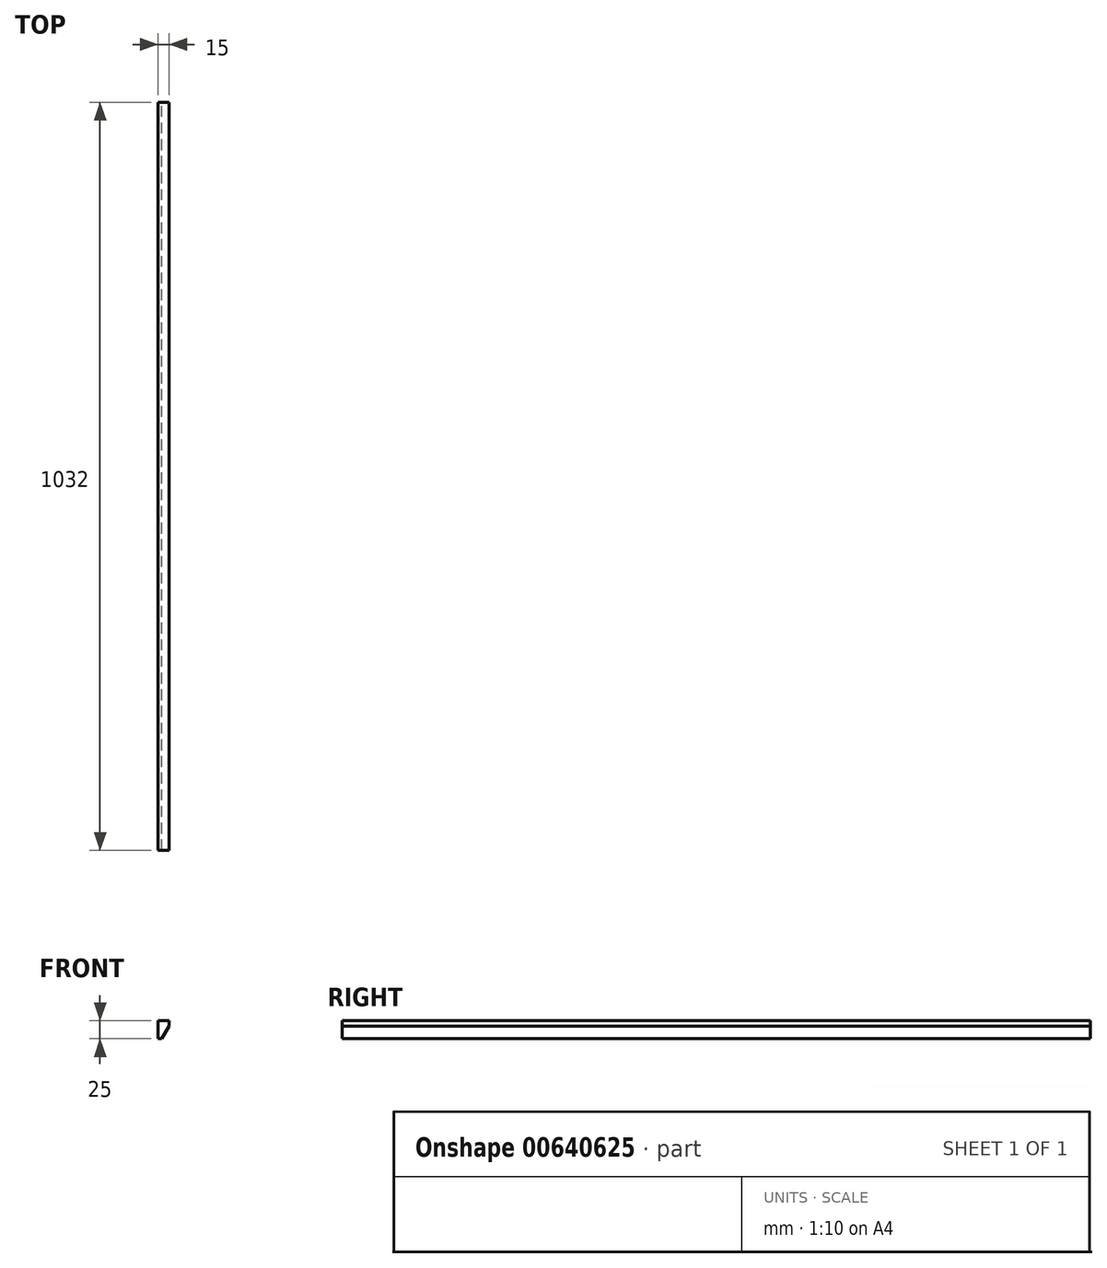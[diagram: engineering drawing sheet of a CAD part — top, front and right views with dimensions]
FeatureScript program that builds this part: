
annotation { "Feature Type Name" : "Feature", "Feature Type Description" : "" }
export const myFeature = defineFeature(function(context is Context, id is Id, definition is map)
    precondition{}
    {
        {
            var Q0;
            Q0=qCreatedBy(makeId("Front.planeOp"),FACE);
            var sketch = newSketch(context, id + "F0", { "sketchPlane" : qUnion([Q0])});
            skLineSegment(sketch, "E0.bottom", {"start": v(0, 0) * mm, "end": v(5, 0) * mm});
            skLineSegment(sketch, "E0.top", {"start": v(0, 25) * mm, "end": v(15, 25) * mm});
            skLineSegment(sketch, "E0.left", {"start": v(0, 0) * mm, "end": v(0, 25) * mm});
            skLineSegment(sketch, "E0.right", {"start": v(15, 17.32) * mm, "end": v(15, 25) * mm});
            skLineSegment(sketch, "E1", {"start": v(5, 0) * mm, "end": v(15, 17.32) * mm});
            skSolve(sketch);
        }
        {
            var Q0;
            Q0 = qSketchRegion(id + "F0", true);
            extrude(context, id + "F1", {"entities" : qUnion([Q0]), "depth" : 1032 * mm, "offsetDistance" : 25 * mm});
        }
    });
